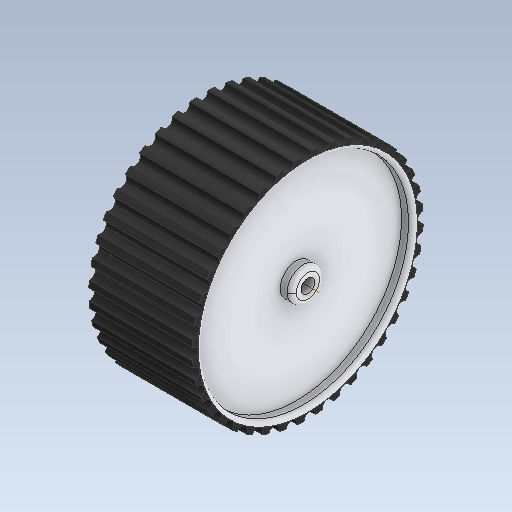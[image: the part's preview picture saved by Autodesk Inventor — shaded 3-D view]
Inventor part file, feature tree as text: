
AUTODESK INVENTOR PART (.ipt)
format: ipt  version: 2020 (Build 240168000, 168)  size: 732,672 bytes
history: native  units: in
note: dims shown in document units (in); Inventor stores cm internally (conversion verified against a paired STEP export)
features: sketch x6, other x5
ambient origin geometry x8: Origin, YZ Plane, XZ Plane, XY Plane, X Axis, Y Axis, Z Axis, Center Point
bodies: Solid1 (feature_tree), Solid2 (feature_tree)
feature tree (11):
  other  "Part2proj.ipt"
  other  "Solid3::Part2proj.ipt"
  other  "Solid4::Part2proj.ipt"
  other  "TaggingFeature1"
  sketch  "Sketch7"  dims[d0=0.3937in]
  sketch  "Sketch8"
  sketch  "Sketch9"
  sketch  "Sketch10"
  sketch  "Sketch13"
  sketch  "Sketch14"
  other  "Work Axis1"
